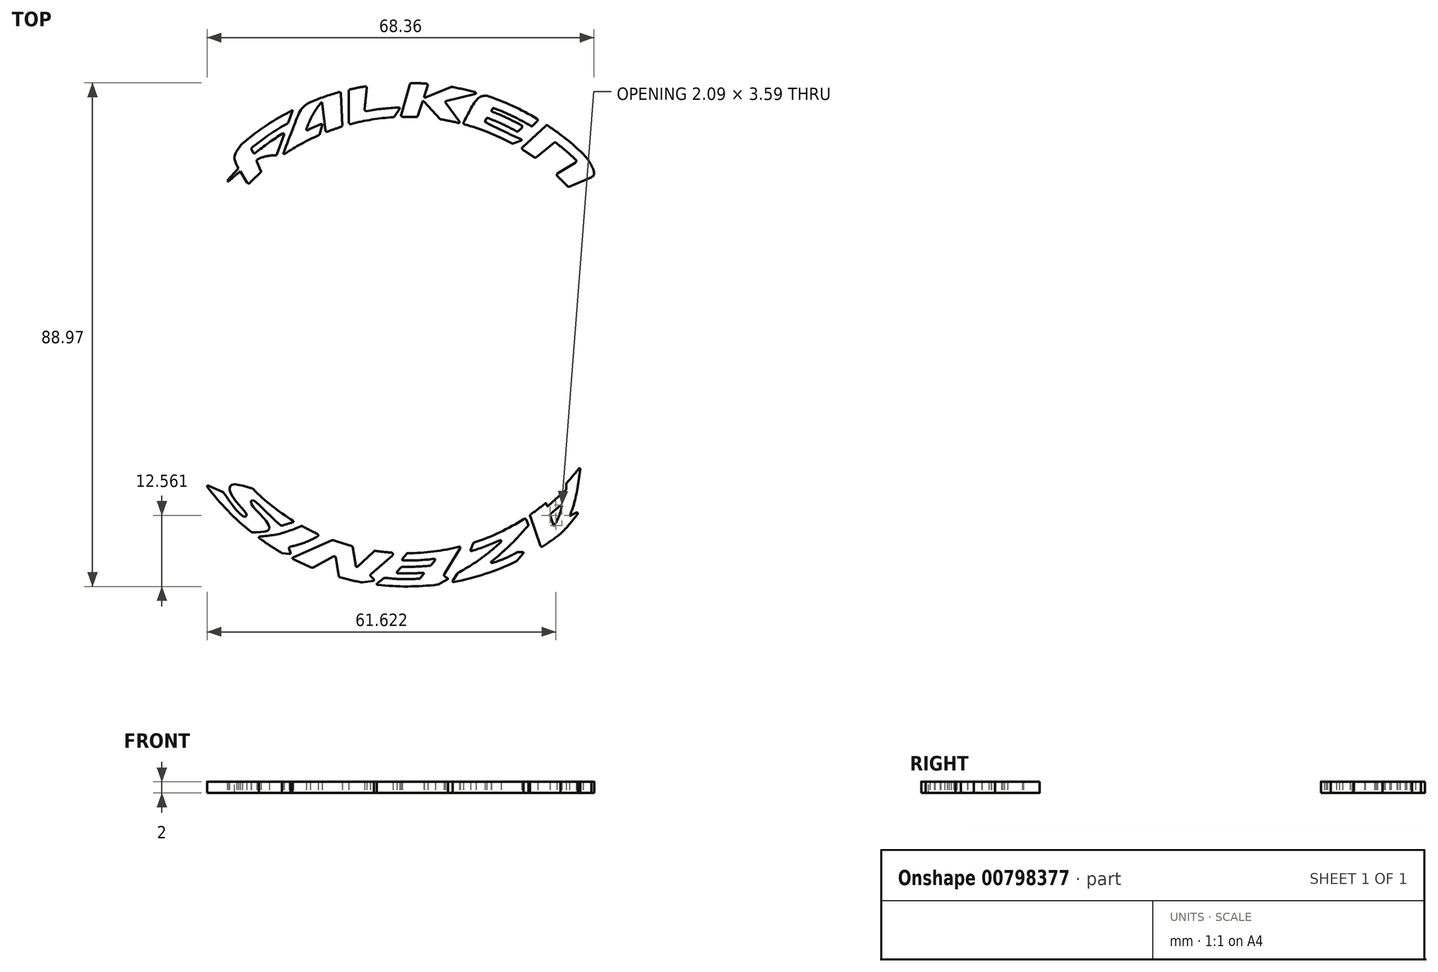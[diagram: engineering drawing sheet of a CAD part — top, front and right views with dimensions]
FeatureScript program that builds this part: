
annotation { "Feature Type Name" : "Feature", "Feature Type Description" : "" }
export const myFeature = defineFeature(function(context is Context, id is Id, definition is map)
    precondition{}
    {
        {
            var Q0;
            Q0=qCreatedBy(makeId("Top.planeOp"),FACE);
            var sketch = newSketch(context, id + "F0", { "sketchPlane" : qUnion([Q0])});
            skArc(sketch, "E0", {"start": v(28.34, 26.57) * mm, "mid": v(27.46, 27.48) * mm, "end": v(26.55, 28.36) * mm});
            skArc(sketch, "E1", {"start": v(31.1, 32.28) * mm, "mid": v(28.1, 34.92) * mm, "end": v(24.88, 37.29) * mm});
            skArc(sketch, "E2.trimOffspring", {"start": v(-25.89, 28.96) * mm, "mid": v(-26.84, 28.08) * mm, "end": v(-27.76, 27.17) * mm});
            skArc(sketch, "E3.trimOffspring", {"start": v(-15.6, 35.57) * mm, "mid": v(-18.67, 34.07) * mm, "end": v(-21.59, 32.3) * mm});
            skArc(sketch, "E4.trimOffspring", {"start": v(-11.66, 37.05) * mm, "mid": v(-12.85, 36.66) * mm, "end": v(-14.03, 36.22) * mm});
            skArc(sketch, "E5.trimOffspring", {"start": v(-2.48, 38.77) * mm, "mid": v(-6.22, 38.34) * mm, "end": v(-9.9, 37.56) * mm});
            skArc(sketch, "E6.trimOffspring", {"start": v(1.61, 38.81) * mm, "mid": v(0.43, 38.84) * mm, "end": v(-0.75, 38.84) * mm});
            skArc(sketch, "E7.trimOffspring", {"start": v(18.47, 34.17) * mm, "mid": v(14.43, 36.07) * mm, "end": v(10.2, 37.48) * mm});
            skArc(sketch, "E8.trimOffspring", {"start": v(22.47, 31.69) * mm, "mid": v(21.48, 32.36) * mm, "end": v(20.48, 33) * mm});
            skArc(sketch, "E9.trimOffspring", {"start": v(9.1, 37.76) * mm, "mid": v(7.58, 38.1) * mm, "end": v(6.04, 38.37) * mm});
            skLineSegment(sketch, "E10", {"start": v(-28.23, 27.22) * mm, "end": v(-29.44, 29.23) * mm});
            skLineSegment(sketch, "E11", {"start": v(28.68, 26.5) * mm, "end": v(32.6, 28.18) * mm});
            skLineSegment(sketch, "E12", {"start": v(-25.81, 29.3) * mm, "end": v(-26.53, 30.94) * mm});
            skLineSegment(sketch, "E13", {"start": v(-20.18, 40.03) * mm, "end": v(-20.97, 37.84) * mm});
            skLineSegment(sketch, "E14", {"start": v(-11.45, 37.35) * mm, "end": v(-11.66, 42.9) * mm});
            skLineSegment(sketch, "E15", {"start": v(-10.28, 37.85) * mm, "end": v(-10.28, 43.4) * mm});
            skLineSegment(sketch, "E16", {"start": v(-7.1, 43.87) * mm, "end": v(-7.5, 40.18) * mm});
            skLineSegment(sketch, "E17", {"start": v(-14.44, 36.47) * mm, "end": v(-14.98, 41.2) * mm});
            skFitSpline(sketch, "E18", {"points": [v(-15.02, 41.58) * mm, v(-16.7, 39.13) * mm, v(-17.9, 36.32) * mm], "startDerivative": vector(-3.62, -4.78) * mm, "endDerivative": vector(-2.11, -5.78) * mm});
            skLineSegment(sketch, "E19", {"start": v(-15.44, 35.77) * mm, "end": v(-15, 37.35) * mm});
            skFitSpline(sketch, "E20", {"points": [v(-23.09, 31.99) * mm, v(-24.2, 31.99) * mm, v(-26.64, 31.2) * mm, v(-31.6, 27.4) * mm], "startDerivative": vector(-4.99, 0.31) * mm, "endDerivative": vector(-10.73, -9.3) * mm});
            skLineSegment(sketch, "E21", {"start": v(-31.6, 27.4) * mm, "end": v(-31.76, 27.6) * mm});
            skFitSpline(sketch, "E22", {"points": [v(-21.98, 32.03) * mm, v(-19.79, 37.78) * mm, v(-18.44, 40.45) * mm, v(-17.08, 41.44) * mm], "startDerivative": vector(5.17, 13.69) * mm, "endDerivative": vector(6.22, 3.24) * mm});
            skArc(sketch, "E23.trimOffspring", {"start": v(-20.18, 40.03) * mm, "mid": v(-24.8, 37.34) * mm, "end": v(-29.05, 34.13) * mm});
            skArc(sketch, "E24.trimOffspring", {"start": v(-21.1, 37.68) * mm, "mid": v(-24.33, 35.69) * mm, "end": v(-27.37, 33.41) * mm});
            skArc(sketch, "E25.trimOffspring", {"start": v(-21.96, 35.9) * mm, "mid": v(-24.42, 34.26) * mm, "end": v(-26.77, 32.46) * mm});
            skLineSegment(sketch, "E26.trimOffspring", {"start": v(-21.74, 35.71) * mm, "end": v(-23.01, 32.2) * mm});
            skLineSegment(sketch, "E27.trimOffspring", {"start": v(-27.24, 32.57) * mm, "end": v(-27.45, 33.06) * mm});
            skLineSegment(sketch, "E28.trimOffspring", {"start": v(-29.75, 29.75) * mm, "end": v(-30.07, 30.28) * mm});
            skArc(sketch, "E29.trimOffspring", {"start": v(-12.04, 43.18) * mm, "mid": v(-14.59, 42.38) * mm, "end": v(-17.08, 41.44) * mm});
            skArc(sketch, "E30.trimOffspring", {"start": v(-15.2, 37.53) * mm, "mid": v(-16.39, 37.03) * mm, "end": v(-17.56, 36.49) * mm});
            skLineSegment(sketch, "E31", {"start": v(-1.04, 39.22) * mm, "end": v(0.5, 44.6) * mm});
            skLineSegment(sketch, "E32", {"start": v(1.9, 39.02) * mm, "end": v(2.72, 41.5) * mm});
            skLineSegment(sketch, "E33", {"start": v(-1.32, 40.23) * mm, "end": v(-2.25, 38.9) * mm});
            skArc(sketch, "E34.trimOffspring", {"start": v(-1.45, 40.47) * mm, "mid": v(-4.3, 40.26) * mm, "end": v(-7.14, 39.86) * mm});
            skArc(sketch, "E35.trimOffspring", {"start": v(-7.45, 44.2) * mm, "mid": v(-8.75, 43.96) * mm, "end": v(-10.05, 43.68) * mm});
            skLineSegment(sketch, "E36", {"start": v(5.87, 38.46) * mm, "end": v(2.97, 41.55) * mm});
            skLineSegment(sketch, "E37", {"start": v(7.76, 44.1) * mm, "end": v(3.24, 42.26) * mm});
            skLineSegment(sketch, "E38", {"start": v(9.26, 38) * mm, "end": v(6.8, 41.36) * mm});
            skLineSegment(sketch, "E39", {"start": v(12.06, 42.88) * mm, "end": v(6.89, 41.6) * mm});
            skLineSegment(sketch, "E40.trimOffspring", {"start": v(3.04, 42.45) * mm, "end": v(3.65, 44.3) * mm});
            skArc(sketch, "E41.trimOffspring", {"start": v(3.38, 44.7) * mm, "mid": v(2.1, 44.77) * mm, "end": v(0.8, 44.82) * mm});
            skFitSpline(sketch, "E42", {"points": [v(9.84, 37.58) * mm, v(11.6, 40.83) * mm, v(12.75, 42.27) * mm, v(13.52, 42.53) * mm, v(14.09, 42.55) * mm], "startDerivative": vector(4.58, 9) * mm, "endDerivative": vector(3.56, -0.32) * mm});
            skArc(sketch, "E43.trimOffspring", {"start": v(12.06, 43.17) * mm, "mid": v(10, 43.7) * mm, "end": v(7.93, 44.12) * mm});
            skLineSegment(sketch, "E44", {"start": v(23, 38.04) * mm, "end": v(22.25, 37.28) * mm});
            skLineSegment(sketch, "E45", {"start": v(20.43, 33.48) * mm, "end": v(24.5, 37.26) * mm});
            skArc(sketch, "E46.trimOffspring", {"start": v(22.94, 38.5) * mm, "mid": v(18.63, 40.77) * mm, "end": v(14.09, 42.55) * mm});
            skArc(sketch, "E47.trimOffspring", {"start": v(21.89, 37.23) * mm, "mid": v(18.69, 38.94) * mm, "end": v(15.35, 40.37) * mm});
            skLineSegment(sketch, "E48", {"start": v(18.7, 34.15) * mm, "end": v(20.14, 34.6) * mm});
            skLineSegment(sketch, "E49", {"start": v(19.69, 36.33) * mm, "end": v(20.26, 36.88) * mm});
            skFitSpline(sketch, "E50", {"points": [v(19.53, 36.17) * mm, v(16.83, 37.55) * mm, v(14.11, 38.68) * mm], "startDerivative": vector(-5.35, 2.93) * mm, "endDerivative": vector(-5.48, 2.09) * mm});
            skFitSpline(sketch, "E51", {"points": [v(20.52, 34.73) * mm, v(16.78, 36.42) * mm, v(13.75, 37.95) * mm], "startDerivative": vector(-7.68, 3.21) * mm, "endDerivative": vector(-5.82, 3.23) * mm});
            skFitSpline(sketch, "E52", {"points": [v(20.55, 37.16) * mm, v(17.46, 38.73) * mm, v(14.85, 39.83) * mm], "startDerivative": vector(-5.98, 3.17) * mm, "endDerivative": vector(-5.42, 2.15) * mm});
            skLineSegment(sketch, "E53", {"start": v(13.82, 38.1) * mm, "end": v(14.04, 38.54) * mm});
            skLineSegment(sketch, "E54", {"start": v(14.96, 40.01) * mm, "end": v(15.14, 40.3) * mm});
            skPoint(sketch, "E55.visualSharp", {"position": v(15.22, 40.42) * mm});
            skArc(sketch, "E55.filletArc", {"start": v(15.35, 40.37) * mm, "mid": v(15.23, 40.37) * mm, "end": v(15.14, 40.3) * mm});
            skArc(sketch, "E56.filletArc", {"start": v(14.96, 40.01) * mm, "mid": v(14.94, 39.86) * mm, "end": v(15.05, 39.75) * mm});
            skArc(sketch, "E57.filletArc", {"start": v(14.27, 38.62) * mm, "mid": v(14.14, 38.62) * mm, "end": v(14.04, 38.54) * mm});
            skArc(sketch, "E58.filletArc", {"start": v(13.82, 38.1) * mm, "mid": v(13.81, 37.97) * mm, "end": v(13.9, 37.87) * mm});
            skLineSegment(sketch, "E59", {"start": v(22.83, 31.7) * mm, "end": v(25.96, 34.23) * mm});
            skLineSegment(sketch, "E60", {"start": v(26.6, 28.83) * mm, "end": v(29.76, 30.78) * mm});
            skArc(sketch, "E61.trimOffspring", {"start": v(29.81, 31.25) * mm, "mid": v(28.11, 32.79) * mm, "end": v(26.33, 34.23) * mm});
            skLineSegment(sketch, "E62", {"start": v(-31.76, 27.6) * mm, "end": v(-29.75, 29.75) * mm});
            skPoint(sketch, "E63.1.internal.snap0", {"position": v(-30.48, 30.96) * mm});
            skFitSpline(sketch, "E63", {"points": [v(-30.07, 30.28) * mm, v(-30.48, 31.62) * mm, v(-30.01, 32.89) * mm, v(-29.05, 34.13) * mm], "startDerivative": vector(-1.88, 4.08) * mm, "endDerivative": vector(3.02, 3.4) * mm});
            skPoint(sketch, "E64.orphan", {"position": v(-31.2, 32.18) * mm});
            skFitSpline(sketch, "E65", {"points": [v(31.1, 32.28) * mm, v(32.1, 31.08) * mm, v(32.98, 29.29) * mm, v(32.98, 28.48) * mm, v(32.6, 28.18) * mm], "startDerivative": vector(3.5, -3.6) * mm, "endDerivative": vector(-2.75, -1.47) * mm});
            skPoint(sketch, "E66.visualSharp", {"position": v(24.68, 37.42) * mm});
            skArc(sketch, "E66.filletArc", {"start": v(24.88, 37.29) * mm, "mid": v(24.69, 37.33) * mm, "end": v(24.5, 37.26) * mm});
            skPoint(sketch, "E67.visualSharp", {"position": v(26.15, 34.38) * mm});
            skArc(sketch, "E67.filletArc", {"start": v(26.33, 34.23) * mm, "mid": v(26.15, 34.3) * mm, "end": v(25.96, 34.23) * mm});
            skPoint(sketch, "E68.visualSharp", {"position": v(22.65, 31.56) * mm});
            skArc(sketch, "E68.filletArc", {"start": v(22.47, 31.69) * mm, "mid": v(22.65, 31.63) * mm, "end": v(22.83, 31.7) * mm});
            skPoint(sketch, "E69.visualSharp", {"position": v(20.14, 33.22) * mm});
            skArc(sketch, "E69.filletArc", {"start": v(20.43, 33.48) * mm, "mid": v(20.34, 33.24) * mm, "end": v(20.48, 33) * mm});
            skPoint(sketch, "E70.visualSharp", {"position": v(30.1, 30.98) * mm});
            skArc(sketch, "E70.filletArc", {"start": v(29.76, 30.78) * mm, "mid": v(29.9, 31) * mm, "end": v(29.81, 31.25) * mm});
            skPoint(sketch, "E71.visualSharp", {"position": v(26.26, 28.63) * mm});
            skArc(sketch, "E71.filletArc", {"start": v(26.6, 28.83) * mm, "mid": v(26.45, 28.6) * mm, "end": v(26.55, 28.36) * mm});
            skPoint(sketch, "E72.visualSharp", {"position": v(28.48, 26.41) * mm});
            skArc(sketch, "E72.filletArc", {"start": v(28.34, 26.57) * mm, "mid": v(28.5, 26.48) * mm, "end": v(28.68, 26.5) * mm});
            skPoint(sketch, "E73.visualSharp", {"position": v(23.27, 38.3) * mm});
            skArc(sketch, "E73.filletArc", {"start": v(23, 38.04) * mm, "mid": v(23.09, 38.29) * mm, "end": v(22.94, 38.5) * mm});
            skPoint(sketch, "E74.visualSharp", {"position": v(22.09, 37.11) * mm});
            skArc(sketch, "E74.filletArc", {"start": v(21.89, 37.23) * mm, "mid": v(22.08, 37.2) * mm, "end": v(22.25, 37.28) * mm});
            skArc(sketch, "E75.filletArc", {"start": v(20.26, 36.88) * mm, "mid": v(20.34, 37.13) * mm, "end": v(20.19, 37.36) * mm});
            skPoint(sketch, "E76.visualSharp", {"position": v(18.59, 34.1) * mm});
            skArc(sketch, "E76.filletArc", {"start": v(18.47, 34.17) * mm, "mid": v(18.59, 34.14) * mm, "end": v(18.7, 34.15) * mm});
            skArc(sketch, "E77.filletArc", {"start": v(19.34, 36.28) * mm, "mid": v(19.52, 36.24) * mm, "end": v(19.69, 36.33) * mm});
            skArc(sketch, "E78.filletArc", {"start": v(10, 37.9) * mm, "mid": v(10, 37.65) * mm, "end": v(10.2, 37.48) * mm});
            skPoint(sketch, "E79.visualSharp", {"position": v(0.57, 44.82) * mm});
            skArc(sketch, "E79.filletArc", {"start": v(0.8, 44.82) * mm, "mid": v(0.62, 44.76) * mm, "end": v(0.5, 44.6) * mm});
            skPoint(sketch, "E80.visualSharp", {"position": v(3.77, 44.67) * mm});
            skArc(sketch, "E80.filletArc", {"start": v(3.65, 44.3) * mm, "mid": v(3.61, 44.56) * mm, "end": v(3.38, 44.7) * mm});
            skPoint(sketch, "E81.visualSharp", {"position": v(1.84, 38.8) * mm});
            skArc(sketch, "E81.filletArc", {"start": v(1.61, 38.81) * mm, "mid": v(1.8, 38.86) * mm, "end": v(1.9, 39.02) * mm});
            skPoint(sketch, "E82.visualSharp", {"position": v(-1.15, 38.83) * mm});
            skArc(sketch, "E82.filletArc", {"start": v(-1.04, 39.22) * mm, "mid": v(-1, 38.96) * mm, "end": v(-0.75, 38.84) * mm});
            skPoint(sketch, "E83.visualSharp", {"position": v(-2.33, 38.78) * mm});
            skArc(sketch, "E83.filletArc", {"start": v(-2.48, 38.77) * mm, "mid": v(-2.35, 38.8) * mm, "end": v(-2.25, 38.9) * mm});
            skPoint(sketch, "E84.visualSharp", {"position": v(-7.53, 39.79) * mm});
            skArc(sketch, "E84.filletArc", {"start": v(-7.5, 40.18) * mm, "mid": v(-7.4, 39.93) * mm, "end": v(-7.14, 39.86) * mm});
            skPoint(sketch, "E85.visualSharp", {"position": v(-10.28, 37.46) * mm});
            skArc(sketch, "E85.filletArc", {"start": v(-10.28, 37.85) * mm, "mid": v(-10.16, 37.61) * mm, "end": v(-9.9, 37.56) * mm});
            skPoint(sketch, "E86.visualSharp", {"position": v(-10.28, 43.63) * mm});
            skArc(sketch, "E86.filletArc", {"start": v(-10.05, 43.68) * mm, "mid": v(-10.22, 43.58) * mm, "end": v(-10.28, 43.4) * mm});
            skPoint(sketch, "E87.visualSharp", {"position": v(-7.06, 44.26) * mm});
            skArc(sketch, "E87.filletArc", {"start": v(-7.1, 43.87) * mm, "mid": v(-7.2, 44.12) * mm, "end": v(-7.45, 44.2) * mm});
            skPoint(sketch, "E88.visualSharp", {"position": v(-11.67, 43.28) * mm});
            skArc(sketch, "E88.filletArc", {"start": v(-11.66, 42.9) * mm, "mid": v(-11.78, 43.13) * mm, "end": v(-12.04, 43.18) * mm});
            skPoint(sketch, "E89.visualSharp", {"position": v(-11.44, 37.12) * mm});
            skArc(sketch, "E89.filletArc", {"start": v(-11.66, 37.05) * mm, "mid": v(-11.5, 37.17) * mm, "end": v(-11.45, 37.35) * mm});
            skPoint(sketch, "E90.visualSharp", {"position": v(-14.4, 36.08) * mm});
            skArc(sketch, "E90.filletArc", {"start": v(-14.44, 36.47) * mm, "mid": v(-14.3, 36.25) * mm, "end": v(-14.03, 36.22) * mm});
            skPoint(sketch, "E91.visualSharp", {"position": v(-15.48, 35.63) * mm});
            skArc(sketch, "E91.filletArc", {"start": v(-15.6, 35.57) * mm, "mid": v(-15.5, 35.65) * mm, "end": v(-15.44, 35.77) * mm});
            skPoint(sketch, "E92.visualSharp", {"position": v(-28.03, 26.89) * mm});
            skArc(sketch, "E92.filletArc", {"start": v(-28.23, 27.22) * mm, "mid": v(-28.01, 27.08) * mm, "end": v(-27.76, 27.17) * mm});
            skPoint(sketch, "E93.visualSharp", {"position": v(-25.73, 29.1) * mm});
            skArc(sketch, "E93.filletArc", {"start": v(-25.89, 28.96) * mm, "mid": v(-25.8, 29.12) * mm, "end": v(-25.81, 29.3) * mm});
            skPoint(sketch, "E94.visualSharp", {"position": v(-21, 37.74) * mm});
            skArc(sketch, "E94.filletArc", {"start": v(-21.1, 37.68) * mm, "mid": v(-21.02, 37.75) * mm, "end": v(-20.97, 37.84) * mm});
            skPoint(sketch, "E95.visualSharp", {"position": v(-27.54, 33.27) * mm});
            skArc(sketch, "E95.filletArc", {"start": v(-27.37, 33.41) * mm, "mid": v(-27.47, 33.25) * mm, "end": v(-27.45, 33.06) * mm});
            skPoint(sketch, "E96.visualSharp", {"position": v(-27.08, 32.2) * mm});
            skArc(sketch, "E96.filletArc", {"start": v(-27.24, 32.57) * mm, "mid": v(-27.03, 32.4) * mm, "end": v(-26.77, 32.46) * mm});
            skArc(sketch, "E97.filletArc", {"start": v(-26.38, 31.33) * mm, "mid": v(-26.53, 31.16) * mm, "end": v(-26.53, 30.94) * mm});
            skArc(sketch, "E98.filletArc", {"start": v(-23.31, 32) * mm, "mid": v(-23.13, 32.05) * mm, "end": v(-23.01, 32.2) * mm});
            skPoint(sketch, "E99.visualSharp", {"position": v(-21.6, 36.11) * mm});
            skArc(sketch, "E99.filletArc", {"start": v(-21.74, 35.71) * mm, "mid": v(-21.78, 35.88) * mm, "end": v(-21.96, 35.9) * mm});
            skPoint(sketch, "E100.visualSharp", {"position": v(-14.92, 37.65) * mm});
            skArc(sketch, "E100.filletArc", {"start": v(-15, 37.35) * mm, "mid": v(-15.04, 37.5) * mm, "end": v(-15.2, 37.53) * mm});
            skArc(sketch, "E101.filletArc", {"start": v(-21.81, 32.47) * mm, "mid": v(-21.76, 32.3) * mm, "end": v(-21.59, 32.3) * mm});
            skArc(sketch, "E102.filletArc", {"start": v(-17.77, 36.67) * mm, "mid": v(-17.73, 36.51) * mm, "end": v(-17.56, 36.49) * mm});
            skArc(sketch, "E103.filletArc", {"start": v(-14.98, 41.2) * mm, "mid": v(-15.09, 41.34) * mm, "end": v(-15.25, 41.28) * mm});
            skPoint(sketch, "E104.visualSharp", {"position": v(-1.15, 40.48) * mm});
            skArc(sketch, "E104.filletArc", {"start": v(-1.32, 40.23) * mm, "mid": v(-1.32, 40.39) * mm, "end": v(-1.45, 40.47) * mm});
            skPoint(sketch, "E105.visualSharp", {"position": v(2.94, 42.14) * mm});
            skArc(sketch, "E105.filletArc", {"start": v(3.04, 42.45) * mm, "mid": v(3.08, 42.3) * mm, "end": v(3.24, 42.26) * mm});
            skPoint(sketch, "E106.visualSharp", {"position": v(2.8, 41.73) * mm});
            skArc(sketch, "E106.filletArc", {"start": v(2.97, 41.55) * mm, "mid": v(2.83, 41.6) * mm, "end": v(2.72, 41.5) * mm});
            skPoint(sketch, "E107.visualSharp", {"position": v(6.67, 41.54) * mm});
            skArc(sketch, "E107.filletArc", {"start": v(6.89, 41.6) * mm, "mid": v(6.78, 41.5) * mm, "end": v(6.8, 41.36) * mm});
            skPoint(sketch, "E108.visualSharp", {"position": v(9.5, 37.67) * mm});
            skArc(sketch, "E108.filletArc", {"start": v(9.1, 37.76) * mm, "mid": v(9.26, 37.83) * mm, "end": v(9.26, 38) * mm});
            skPoint(sketch, "E109.visualSharp", {"position": v(12.6, 43.02) * mm});
            skArc(sketch, "E109.filletArc", {"start": v(12.06, 42.88) * mm, "mid": v(12.17, 43.02) * mm, "end": v(12.06, 43.17) * mm});
            skArc(sketch, "E110.filletArc", {"start": v(20.14, 34.6) * mm, "mid": v(20.24, 34.74) * mm, "end": v(20.15, 34.89) * mm});
            skPoint(sketch, "E111.visualSharp", {"position": v(7.84, 44.13) * mm});
            skArc(sketch, "E111.filletArc", {"start": v(7.93, 44.12) * mm, "mid": v(7.84, 44.12) * mm, "end": v(7.76, 44.1) * mm});
            skPoint(sketch, "E112.visualSharp", {"position": v(5.94, 38.39) * mm});
            skArc(sketch, "E112.filletArc", {"start": v(5.87, 38.46) * mm, "mid": v(5.95, 38.4) * mm, "end": v(6.04, 38.37) * mm});
            skSolve(sketch);
        }
        {
            var Q0;
            Q0=qSketchRegion(id+"F0",true);
            extrude(context, id + "F1", {"entities" : qUnion([Q0]), "depth" : 2 * mm, "offsetDistance" : 25 * mm});
        }
        {
            var Q0;
            Q0=qCreatedBy(makeId("Top.planeOp"),FACE);
            var sketch = newSketch(context, id + "F2", { "sketchPlane" : qUnion([Q0])});
            skArc(sketch, "E113", {"start": v(-27.2, -26.93) * mm, "mid": v(-23.83, -29.95) * mm, "end": v(-20.13, -32.55) * mm});
            skArc(sketch, "E114", {"start": v(-35.28, -26.56) * mm, "mid": v(-31.65, -30.79) * mm, "end": v(-27.52, -34.53) * mm});
            skArc(sketch, "E115", {"start": v(-0.78, -40.67) * mm, "mid": v(1.64, -40.65) * mm, "end": v(4.05, -40.48) * mm});
            skArc(sketch, "E116", {"start": v(-1.66, -41.8) * mm, "mid": v(0.57, -41.83) * mm, "end": v(2.8, -41.74) * mm});
            skArc(sketch, "E117.trimOffspring", {"start": v(28.17, -25.9) * mm, "mid": v(29.3, -24.63) * mm, "end": v(30.35, -23.32) * mm});
            skArc(sketch, "E118.trimOffspring", {"start": v(21.87, -31.4) * mm, "mid": v(23.15, -30.48) * mm, "end": v(24.4, -29.5) * mm});
            skArc(sketch, "E119.trimOffspring", {"start": v(11.85, -36.4) * mm, "mid": v(16.4, -34.59) * mm, "end": v(20.66, -32.22) * mm});
            skArc(sketch, "E120.trimOffspring", {"start": v(0.15, -38.27) * mm, "mid": v(4.72, -37.98) * mm, "end": v(9.23, -37.14) * mm});
            skArc(sketch, "E121.trimOffspring", {"start": v(-5.6, -37.86) * mm, "mid": v(-4.2, -38.04) * mm, "end": v(-2.77, -38.17) * mm});
            skArc(sketch, "E122.trimOffspring", {"start": v(-13.04, -35.98) * mm, "mid": v(-11.43, -36.53) * mm, "end": v(-9.79, -37) * mm});
            skArc(sketch, "E123.trimOffspring", {"start": v(-18.5, -33.5) * mm, "mid": v(-17.2, -34.2) * mm, "end": v(-15.87, -34.83) * mm});
            skFitSpline(sketch, "E124", {"points": [v(30.7, -22.86) * mm, v(29.74, -28.66) * mm, v(28.73, -31.75) * mm], "startDerivative": vector(-1.46, -10.93) * mm, "endDerivative": vector(-2.51, -6.64) * mm});
            skLineSegment(sketch, "E125", {"start": v(28.73, -31.75) * mm, "end": v(29.94, -31.12) * mm});
            skFitSpline(sketch, "E126", {"points": [v(30.5, -30.82) * mm, v(28.94, -32.88) * mm, v(27.11, -34.85) * mm], "startDerivative": vector(-3, -4.24) * mm, "endDerivative": vector(-3.82, -3.76) * mm});
            skLineSegment(sketch, "E127", {"start": v(21.76, -31.75) * mm, "end": v(23.54, -36.92) * mm});
            skLineSegment(sketch, "E128", {"start": v(24.63, -29.56) * mm, "end": v(24.72, -29.84) * mm});
            skLineSegment(sketch, "E129", {"start": v(25.33, -31.36) * mm, "end": v(27.11, -29.83) * mm});
            skFitSpline(sketch, "E130", {"points": [v(27.45, -29.54) * mm, v(26.94, -31.48) * mm, v(25.93, -33.62) * mm], "startDerivative": vector(-0.9, -4.23) * mm, "endDerivative": vector(-2.18, -4.16) * mm});
            skLineSegment(sketch, "E131", {"start": v(28.13, -26) * mm, "end": v(28.13, -26.96) * mm});
            skLineSegment(sketch, "E132", {"start": v(28.09, -27.07) * mm, "end": v(24.96, -29.9) * mm});
            skLineSegment(sketch, "E133.trimOffspring", {"start": v(25.27, -31.57) * mm, "end": v(25.82, -33.28) * mm});
            skLineSegment(sketch, "E134", {"start": v(-35.1, -26.33) * mm, "end": v(-32.53, -27.48) * mm});
            skLineSegment(sketch, "E135", {"start": v(11.67, -36.57) * mm, "end": v(11.24, -37.69) * mm});
            skLineSegment(sketch, "E136", {"start": v(8.09, -43.15) * mm, "end": v(8.87, -41.87) * mm});
            skFitSpline(sketch, "E137", {"points": [v(8.9, -41.8) * mm, v(13.04, -39.23) * mm, v(16.54, -36.3) * mm, v(17.03, -35.71) * mm], "startDerivative": vector(9.56, 5.46) * mm, "endDerivative": vector(1.94, 3.07) * mm});
            skLineSegment(sketch, "E138", {"start": v(9.4, -37.37) * mm, "end": v(6.58, -41.96) * mm});
            skLineSegment(sketch, "E139", {"start": v(6.68, -42.37) * mm, "end": v(7.14, -42.65) * mm});
            skLineSegment(sketch, "E140", {"start": v(7.13, -42.91) * mm, "end": v(5.53, -43.78) * mm});
            skArc(sketch, "E141.trimOffspring", {"start": v(8.24, -43.38) * mm, "mid": v(13.87, -41.92) * mm, "end": v(19.26, -39.73) * mm});
            skArc(sketch, "E142.trimOffspring", {"start": v(11.42, -37.88) * mm, "mid": v(13.97, -37.02) * mm, "end": v(16.45, -35.99) * mm});
            skFitSpline(sketch, "E143", {"points": [v(21.72, -33.07) * mm, v(18.37, -36.68) * mm, v(14.35, -40.24) * mm], "startDerivative": vector(-6.63, -7.5) * mm, "endDerivative": vector(-8.13, -6.86) * mm});
            skFitSpline(sketch, "E144", {"points": [v(14.35, -40.24) * mm, v(17.4, -39.16) * mm, v(19.48, -38.1) * mm], "startDerivative": vector(5.94, 1.92) * mm, "endDerivative": vector(4.27, 2.38) * mm});
            skLineSegment(sketch, "E145", {"start": v(19.56, -38.1) * mm, "end": v(20.43, -38.1) * mm});
            skLineSegment(sketch, "E146", {"start": v(20.55, -38.34) * mm, "end": v(19.35, -39.66) * mm});
            skArc(sketch, "E147.trimOffspring", {"start": v(23.98, -37.07) * mm, "mid": v(25.57, -36) * mm, "end": v(27.11, -34.85) * mm});
            skLineSegment(sketch, "E148", {"start": v(4.95, -39.52) * mm, "end": v(4.25, -40.37) * mm});
            skLineSegment(sketch, "E149", {"start": v(-1, -40.76) * mm, "end": v(-1.77, -41.55) * mm});
            skLineSegment(sketch, "E150", {"start": v(-0.09, -38.39) * mm, "end": v(-0.82, -39.32) * mm});
            skLineSegment(sketch, "E151", {"start": v(-2.6, -38.7) * mm, "end": v(-6.36, -41.98) * mm});
            skLineSegment(sketch, "E152", {"start": v(-6.37, -42.42) * mm, "end": v(-5.86, -42.91) * mm});
            skLineSegment(sketch, "E153", {"start": v(-5.95, -43.17) * mm, "end": v(-7.8, -43.44) * mm});
            skLineSegment(sketch, "E154", {"start": v(-5.27, -43.58) * mm, "end": v(-4.14, -42.7) * mm});
            skFitSpline(sketch, "E155", {"points": [v(-4.05, -42.62) * mm, v(-0.56, -42.86) * mm, v(2.29, -42.77) * mm], "startDerivative": vector(6.81, -0.64) * mm, "endDerivative": vector(5.85, 0.36) * mm});
            skArc(sketch, "E156.trimOffspring", {"start": v(-5.2, -43.85) * mm, "mid": v(0.12, -44.15) * mm, "end": v(5.42, -43.82) * mm});
            skArc(sketch, "E157.trimOffspring", {"start": v(-0.7, -39.56) * mm, "mid": v(2.06, -39.51) * mm, "end": v(4.82, -39.27) * mm});
            skLineSegment(sketch, "E158", {"start": v(-13.27, -35.99) * mm, "end": v(-20.14, -39.02) * mm});
            skLineSegment(sketch, "E159", {"start": v(-9.57, -37.24) * mm, "end": v(-9, -40.59) * mm});
            skLineSegment(sketch, "E160", {"start": v(-5.85, -37.94) * mm, "end": v(-8.75, -40.67) * mm});
            skLineSegment(sketch, "E161", {"start": v(-13, -38.87) * mm, "end": v(-16.6, -40.8) * mm});
            skLineSegment(sketch, "E162", {"start": v(-12.56, -39.1) * mm, "end": v(-12.06, -42.3) * mm});
            skArc(sketch, "E163.trimOffspring", {"start": v(-11.84, -42.54) * mm, "mid": v(-9.88, -43.03) * mm, "end": v(-7.9, -43.44) * mm});
            skFitSpline(sketch, "E164", {"points": [v(-15.3, -35.08) * mm, v(-18.14, -36.41) * mm, v(-20.94, -37.22) * mm], "startDerivative": vector(-5.54, -2.77) * mm, "endDerivative": vector(-5.75, -1.5) * mm});
            skLineSegment(sketch, "E165", {"start": v(-20.83, -37.53) * mm, "end": v(-20.59, -38.22) * mm});
            skLineSegment(sketch, "E166", {"start": v(-20.75, -38.42) * mm, "end": v(-22.07, -38.24) * mm});
            skArc(sketch, "E167.trimOffspring", {"start": v(-20.15, -39.29) * mm, "mid": v(-18.51, -40.08) * mm, "end": v(-16.85, -40.81) * mm});
            skFitSpline(sketch, "E168", {"points": [v(-26.42, -35.38) * mm, v(-22.38, -34.8) * mm, v(-18.62, -33.44) * mm], "startDerivative": vector(8.12, 0.66) * mm, "endDerivative": vector(7.42, 3.16) * mm});
            skLineSegment(sketch, "E169.trimOffspring", {"start": v(2.93, -41.99) * mm, "end": v(2.37, -42.67) * mm});
            skFitSpline(sketch, "E170", {"points": [v(-27.43, -34.6) * mm, v(-25.35, -34.46) * mm, v(-24.43, -34.12) * mm, v(-24.39, -33.4) * mm, v(-25.9, -31.46) * mm, v(-27.47, -29.58) * mm, v(-27.5, -28.97) * mm, v(-27.02, -29) * mm, v(-25.71, -30.16) * mm, v(-22.22, -33.44) * mm], "startDerivative": vector(17.57, 0.48) * mm, "endDerivative": vector(20.31, -18.62) * mm});
            skLineSegment(sketch, "E171", {"start": v(-22.06, -33.4) * mm, "end": v(-20.17, -32.82) * mm});
            skFitSpline(sketch, "E172", {"points": [v(-27.25, -26.87) * mm, v(-29.61, -26.22) * mm, v(-30.87, -26.14) * mm, v(-31.3, -26.56) * mm, v(-31.22, -27.5) * mm, v(-29.92, -29.53) * mm, v(-28.63, -30.94) * mm, v(-28.35, -31.47) * mm, v(-28.43, -31.76) * mm, v(-28.94, -31.78) * mm, v(-30.78, -29.8) * mm, v(-32.46, -27.5) * mm], "startDerivative": vector(-20.2, 6.1) * mm, "endDerivative": vector(-11.92, 16.52) * mm});
            skArc(sketch, "E173.trimOffspring", {"start": v(-26.1, -35.62) * mm, "mid": v(-24.12, -36.98) * mm, "end": v(-22.07, -38.24) * mm});
            skLineSegment(sketch, "E174", {"start": v(21.1, -32.36) * mm, "end": v(21.41, -33.17) * mm});
            skArc(sketch, "E175.filletArc", {"start": v(-18.5, -33.5) * mm, "mid": v(-18.62, -33.47) * mm, "end": v(-18.76, -33.5) * mm});
            skPoint(sketch, "E176.visualSharp", {"position": v(-13.16, -35.94) * mm});
            skArc(sketch, "E176.filletArc", {"start": v(-13.04, -35.98) * mm, "mid": v(-13.16, -35.96) * mm, "end": v(-13.27, -35.99) * mm});
            skPoint(sketch, "E177.visualSharp", {"position": v(-9.6, -37.05) * mm});
            skArc(sketch, "E177.filletArc", {"start": v(-9.57, -37.24) * mm, "mid": v(-9.64, -37.09) * mm, "end": v(-9.79, -37) * mm});
            skPoint(sketch, "E178.visualSharp", {"position": v(-2.05, -38.22) * mm});
            skArc(sketch, "E178.filletArc", {"start": v(-2.6, -38.7) * mm, "mid": v(-2.51, -38.38) * mm, "end": v(-2.77, -38.17) * mm});
            skPoint(sketch, "E179.visualSharp", {"position": v(-12.62, -38.67) * mm});
            skArc(sketch, "E179.filletArc", {"start": v(-12.56, -39.1) * mm, "mid": v(-12.72, -38.87) * mm, "end": v(-13, -38.87) * mm});
            skArc(sketch, "E180.filletArc", {"start": v(-15.86, -35.37) * mm, "mid": v(-15.7, -35.1) * mm, "end": v(-15.87, -34.83) * mm});
            skArc(sketch, "E181.filletArc", {"start": v(-20.62, -37.14) * mm, "mid": v(-20.81, -37.29) * mm, "end": v(-20.83, -37.53) * mm});
            skArc(sketch, "E182.filletArc", {"start": v(-22.35, -33.33) * mm, "mid": v(-22.21, -33.4) * mm, "end": v(-22.06, -33.4) * mm});
            skArc(sketch, "E183.filletArc", {"start": v(-32.41, -27.57) * mm, "mid": v(-32.47, -27.52) * mm, "end": v(-32.53, -27.48) * mm});
            skArc(sketch, "E184.filletArc", {"start": v(-27.2, -26.93) * mm, "mid": v(-27.26, -26.88) * mm, "end": v(-27.32, -26.85) * mm});
            skArc(sketch, "E185.filletArc", {"start": v(-27.52, -34.53) * mm, "mid": v(-27.43, -34.58) * mm, "end": v(-27.32, -34.6) * mm});
            skPoint(sketch, "E186.visualSharp", {"position": v(-16.72, -40.87) * mm});
            skArc(sketch, "E186.filletArc", {"start": v(-16.85, -40.81) * mm, "mid": v(-16.72, -40.83) * mm, "end": v(-16.6, -40.8) * mm});
            skPoint(sketch, "E187.visualSharp", {"position": v(-12.03, -42.48) * mm});
            skArc(sketch, "E187.filletArc", {"start": v(-12.06, -42.3) * mm, "mid": v(-11.98, -42.45) * mm, "end": v(-11.84, -42.54) * mm});
            skPoint(sketch, "E188.visualSharp", {"position": v(-7.86, -43.45) * mm});
            skArc(sketch, "E188.filletArc", {"start": v(-7.9, -43.44) * mm, "mid": v(-7.86, -43.44) * mm, "end": v(-7.8, -43.44) * mm});
            skPoint(sketch, "E189.visualSharp", {"position": v(-6.6, -42.2) * mm});
            skArc(sketch, "E189.filletArc", {"start": v(-6.36, -41.98) * mm, "mid": v(-6.46, -42.2) * mm, "end": v(-6.37, -42.42) * mm});
            skPoint(sketch, "E190.visualSharp", {"position": v(-5.75, -37.84) * mm});
            skArc(sketch, "E190.filletArc", {"start": v(-5.6, -37.86) * mm, "mid": v(-5.74, -37.87) * mm, "end": v(-5.85, -37.94) * mm});
            skPoint(sketch, "E191.visualSharp", {"position": v(4.17, -40.47) * mm});
            skArc(sketch, "E191.filletArc", {"start": v(4.05, -40.48) * mm, "mid": v(4.16, -40.44) * mm, "end": v(4.25, -40.37) * mm});
            skPoint(sketch, "E192.visualSharp", {"position": v(0, -38.27) * mm});
            skArc(sketch, "E192.filletArc", {"start": v(0.15, -38.27) * mm, "mid": v(0.01, -38.3) * mm, "end": v(-0.09, -38.39) * mm});
            skArc(sketch, "E193.filletArc", {"start": v(2.16, -42.77) * mm, "mid": v(2.27, -42.74) * mm, "end": v(2.37, -42.67) * mm});
            skPoint(sketch, "E194.visualSharp", {"position": v(5.48, -43.81) * mm});
            skArc(sketch, "E194.filletArc", {"start": v(5.42, -43.82) * mm, "mid": v(5.48, -43.8) * mm, "end": v(5.53, -43.78) * mm});
            skPoint(sketch, "E195.visualSharp", {"position": v(6.43, -42.21) * mm});
            skArc(sketch, "E195.filletArc", {"start": v(6.58, -41.96) * mm, "mid": v(6.55, -42.19) * mm, "end": v(6.68, -42.37) * mm});
            skArc(sketch, "E196.filletArc", {"start": v(-3.93, -42.63) * mm, "mid": v(-4.04, -42.64) * mm, "end": v(-4.14, -42.7) * mm});
            skPoint(sketch, "E197.visualSharp", {"position": v(-0.91, -40.67) * mm});
            skArc(sketch, "E197.filletArc", {"start": v(-0.78, -40.67) * mm, "mid": v(-0.9, -40.7) * mm, "end": v(-1, -40.76) * mm});
            skArc(sketch, "E198.filletArc", {"start": v(8.98, -41.77) * mm, "mid": v(8.92, -41.81) * mm, "end": v(8.87, -41.87) * mm});
            skPoint(sketch, "E199.visualSharp", {"position": v(11.72, -36.44) * mm});
            skArc(sketch, "E199.filletArc", {"start": v(11.85, -36.4) * mm, "mid": v(11.74, -36.46) * mm, "end": v(11.67, -36.57) * mm});
            skPoint(sketch, "E200.visualSharp", {"position": v(19.31, -39.7) * mm});
            skArc(sketch, "E200.filletArc", {"start": v(19.26, -39.73) * mm, "mid": v(19.3, -39.7) * mm, "end": v(19.35, -39.66) * mm});
            skArc(sketch, "E201.filletArc", {"start": v(19.56, -38.1) * mm, "mid": v(19.48, -38.1) * mm, "end": v(19.41, -38.13) * mm});
            skPoint(sketch, "E202.visualSharp", {"position": v(20.97, -32.02) * mm});
            skArc(sketch, "E202.filletArc", {"start": v(21.1, -32.36) * mm, "mid": v(20.92, -32.18) * mm, "end": v(20.66, -32.22) * mm});
            skPoint(sketch, "E203.visualSharp", {"position": v(21.68, -31.54) * mm});
            skArc(sketch, "E203.filletArc", {"start": v(21.87, -31.4) * mm, "mid": v(21.76, -31.56) * mm, "end": v(21.76, -31.75) * mm});
            skPoint(sketch, "E204.visualSharp", {"position": v(23.66, -37.28) * mm});
            skArc(sketch, "E204.filletArc", {"start": v(23.54, -36.92) * mm, "mid": v(23.72, -37.1) * mm, "end": v(23.98, -37.07) * mm});
            skPoint(sketch, "E205.visualSharp", {"position": v(25.23, -31.45) * mm});
            skArc(sketch, "E205.filletArc", {"start": v(25.33, -31.36) * mm, "mid": v(25.27, -31.46) * mm, "end": v(25.27, -31.57) * mm});
            skPoint(sketch, "E206.visualSharp", {"position": v(21.48, -33.34) * mm});
            skArc(sketch, "E206.filletArc", {"start": v(21.36, -33.48) * mm, "mid": v(21.43, -33.33) * mm, "end": v(21.41, -33.17) * mm});
            skArc(sketch, "E207.filletArc", {"start": v(14.94, -39.75) * mm, "mid": v(14.9, -39.93) * mm, "end": v(15.08, -40) * mm});
            skPoint(sketch, "E208.visualSharp", {"position": v(20.77, -38.1) * mm});
            skArc(sketch, "E208.filletArc", {"start": v(20.55, -38.34) * mm, "mid": v(20.57, -38.18) * mm, "end": v(20.43, -38.1) * mm});
            skPoint(sketch, "E209.visualSharp", {"position": v(11.13, -37.97) * mm});
            skArc(sketch, "E209.filletArc", {"start": v(11.24, -37.69) * mm, "mid": v(11.27, -37.84) * mm, "end": v(11.42, -37.88) * mm});
            skPoint(sketch, "E210.visualSharp", {"position": v(7.91, -43.44) * mm});
            skArc(sketch, "E210.filletArc", {"start": v(8.09, -43.15) * mm, "mid": v(8.1, -43.32) * mm, "end": v(8.24, -43.38) * mm});
            skArc(sketch, "E211.filletArc", {"start": v(30.13, -31.34) * mm, "mid": v(30.12, -31.15) * mm, "end": v(29.94, -31.12) * mm});
            skArc(sketch, "E212.filletArc", {"start": v(25.82, -33.28) * mm, "mid": v(25.95, -33.39) * mm, "end": v(26.1, -33.3) * mm});
            skArc(sketch, "E213.filletArc", {"start": v(27.36, -29.97) * mm, "mid": v(27.29, -29.81) * mm, "end": v(27.11, -29.83) * mm});
            skArc(sketch, "E214.filletArc", {"start": v(30.62, -23.43) * mm, "mid": v(30.53, -23.27) * mm, "end": v(30.35, -23.32) * mm});
            skPoint(sketch, "E215.visualSharp", {"position": v(24.56, -29.35) * mm});
            skArc(sketch, "E215.filletArc", {"start": v(24.63, -29.56) * mm, "mid": v(24.53, -29.47) * mm, "end": v(24.4, -29.5) * mm});
            skPoint(sketch, "E216.visualSharp", {"position": v(24.8, -30.07) * mm});
            skArc(sketch, "E216.filletArc", {"start": v(24.72, -29.84) * mm, "mid": v(24.82, -29.94) * mm, "end": v(24.96, -29.9) * mm});
            skPoint(sketch, "E217.visualSharp", {"position": v(28.13, -27.03) * mm});
            skArc(sketch, "E217.filletArc", {"start": v(28.09, -27.07) * mm, "mid": v(28.12, -27.02) * mm, "end": v(28.13, -26.96) * mm});
            skPoint(sketch, "E218.visualSharp", {"position": v(28.13, -25.95) * mm});
            skArc(sketch, "E218.filletArc", {"start": v(28.17, -25.9) * mm, "mid": v(28.14, -25.95) * mm, "end": v(28.13, -26) * mm});
            skArc(sketch, "E219.filletArc", {"start": v(16.62, -36.23) * mm, "mid": v(16.63, -36.04) * mm, "end": v(16.45, -35.99) * mm});
            skPoint(sketch, "E220.visualSharp", {"position": v(9.59, -37.05) * mm});
            skArc(sketch, "E220.filletArc", {"start": v(9.4, -37.37) * mm, "mid": v(9.39, -37.2) * mm, "end": v(9.23, -37.14) * mm});
            skPoint(sketch, "E221.visualSharp", {"position": v(5.2, -39.22) * mm});
            skArc(sketch, "E221.filletArc", {"start": v(4.95, -39.52) * mm, "mid": v(4.97, -39.35) * mm, "end": v(4.82, -39.27) * mm});
            skPoint(sketch, "E222.visualSharp", {"position": v(7.36, -42.79) * mm});
            skArc(sketch, "E222.filletArc", {"start": v(7.13, -42.91) * mm, "mid": v(7.21, -42.78) * mm, "end": v(7.14, -42.65) * mm});
            skPoint(sketch, "E223.visualSharp", {"position": v(-2, -41.79) * mm});
            skArc(sketch, "E223.filletArc", {"start": v(-1.77, -41.55) * mm, "mid": v(-1.8, -41.7) * mm, "end": v(-1.66, -41.8) * mm});
            skPoint(sketch, "E224.visualSharp", {"position": v(-1, -39.55) * mm});
            skArc(sketch, "E224.filletArc", {"start": v(-0.82, -39.32) * mm, "mid": v(-0.84, -39.47) * mm, "end": v(-0.7, -39.56) * mm});
            skPoint(sketch, "E225.visualSharp", {"position": v(3.15, -41.72) * mm});
            skArc(sketch, "E225.filletArc", {"start": v(2.93, -41.99) * mm, "mid": v(2.95, -41.82) * mm, "end": v(2.8, -41.74) * mm});
            skPoint(sketch, "E226.visualSharp", {"position": v(-5.55, -43.8) * mm});
            skArc(sketch, "E226.filletArc", {"start": v(-5.27, -43.58) * mm, "mid": v(-5.32, -43.74) * mm, "end": v(-5.2, -43.85) * mm});
            skPoint(sketch, "E227.visualSharp", {"position": v(-5.65, -43.12) * mm});
            skArc(sketch, "E227.filletArc", {"start": v(-5.95, -43.17) * mm, "mid": v(-5.83, -43.06) * mm, "end": v(-5.86, -42.91) * mm});
            skPoint(sketch, "E228.visualSharp", {"position": v(-8.95, -40.87) * mm});
            skArc(sketch, "E228.filletArc", {"start": v(-9, -40.59) * mm, "mid": v(-8.9, -40.7) * mm, "end": v(-8.75, -40.67) * mm});
            skPoint(sketch, "E229.visualSharp", {"position": v(-20.43, -39.14) * mm});
            skArc(sketch, "E229.filletArc", {"start": v(-20.14, -39.02) * mm, "mid": v(-20.23, -39.15) * mm, "end": v(-20.15, -39.29) * mm});
            skPoint(sketch, "E230.visualSharp", {"position": v(-20.5, -38.45) * mm});
            skArc(sketch, "E230.filletArc", {"start": v(-20.75, -38.42) * mm, "mid": v(-20.61, -38.36) * mm, "end": v(-20.59, -38.22) * mm});
            skArc(sketch, "E231.filletArc", {"start": v(-26.02, -35.35) * mm, "mid": v(-26.15, -35.45) * mm, "end": v(-26.1, -35.62) * mm});
            skPoint(sketch, "E232.visualSharp", {"position": v(-19.85, -32.72) * mm});
            skArc(sketch, "E232.filletArc", {"start": v(-20.17, -32.82) * mm, "mid": v(-20.06, -32.7) * mm, "end": v(-20.13, -32.55) * mm});
            skPoint(sketch, "E233.visualSharp", {"position": v(-35.62, -26.1) * mm});
            skArc(sketch, "E233.filletArc", {"start": v(-35.1, -26.33) * mm, "mid": v(-35.27, -26.37) * mm, "end": v(-35.28, -26.56) * mm});
            skSolve(sketch);
        }
        {
            var Q0;
            Q0=qSketchRegion(id+"F2",true);
            extrude(context, id + "F3", {"entities" : qUnion([Q0]), "depth" : 2 * mm, "offsetDistance" : 25 * mm});
        }
    });
